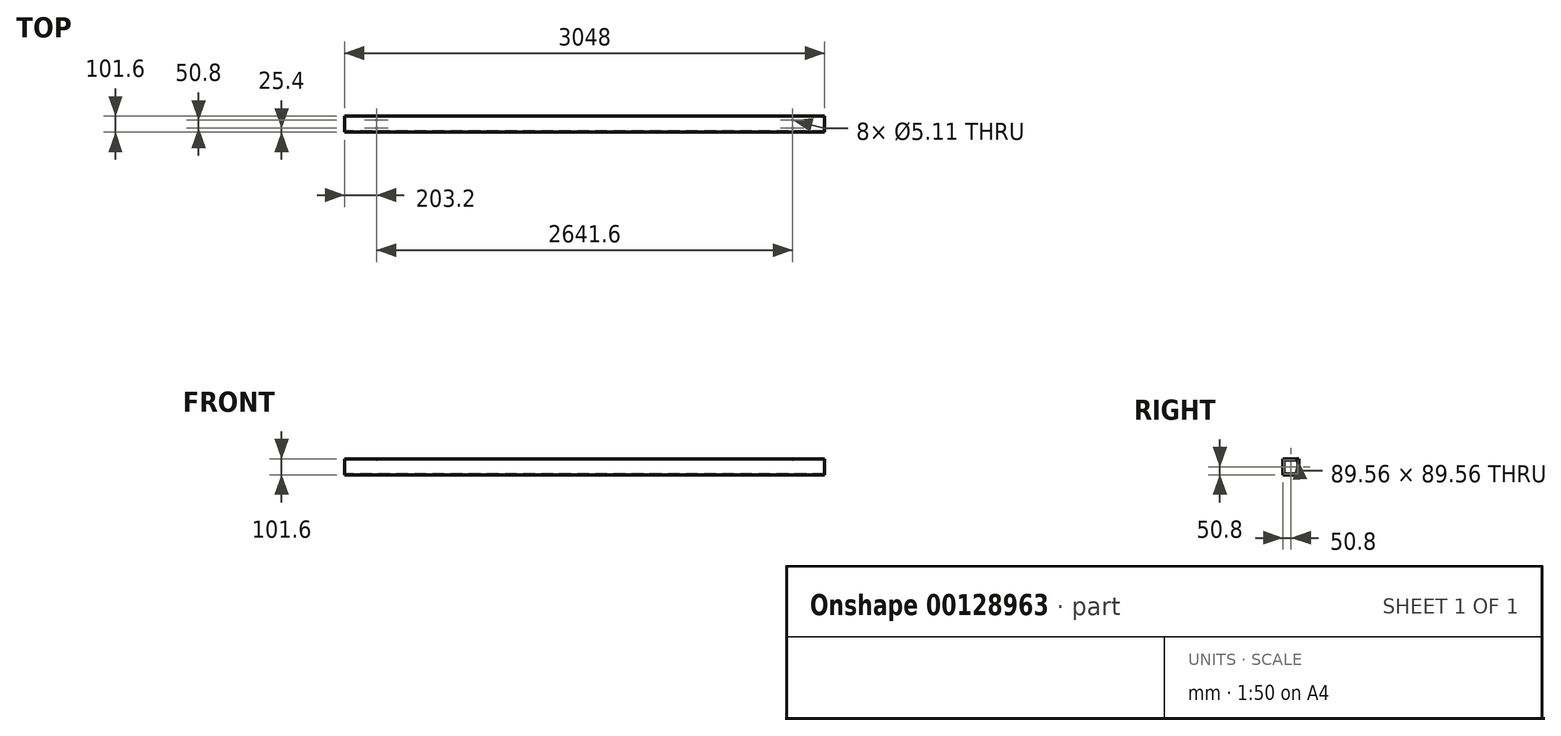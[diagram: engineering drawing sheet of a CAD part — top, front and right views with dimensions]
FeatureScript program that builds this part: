
annotation { "Feature Type Name" : "Feature", "Feature Type Description" : "" }
export const myFeature = defineFeature(function(context is Context, id is Id, definition is map)
    precondition{}
    {
        {
            var Q0;
            Q0=qCreatedBy(makeId("Right.planeOp"),FACE);
            var sketch = newSketch(context, id + "F0", { "sketchPlane" : qUnion([Q0])});
            skLineSegment(sketch, "E0.bottom", {"start": v(50.8, 50.8) * mm, "end": v(-50.8, 50.8) * mm});
            skLineSegment(sketch, "E0.top", {"start": v(50.8, -50.8) * mm, "end": v(-50.8, -50.8) * mm});
            skLineSegment(sketch, "E0.left", {"start": v(50.8, 50.8) * mm, "end": v(50.8, -50.8) * mm});
            skLineSegment(sketch, "E0.right", {"start": v(-50.8, 50.8) * mm, "end": v(-50.8, -50.8) * mm});
            skPoint(sketch, "E0.middle", {"position": v(0, 0) * mm});
            skLineSegment(sketch, "E1.bottom", {"start": v(44.78, 44.78) * mm, "end": v(-44.78, 44.78) * mm});
            skLineSegment(sketch, "E1.top", {"start": v(44.78, -44.78) * mm, "end": v(-44.78, -44.78) * mm});
            skLineSegment(sketch, "E1.left", {"start": v(44.78, 44.78) * mm, "end": v(44.78, -44.78) * mm});
            skLineSegment(sketch, "E1.right", {"start": v(-44.78, 44.78) * mm, "end": v(-44.78, -44.78) * mm});
            skSolve(sketch);
        }
        {
            var Q0;
            Q0=makeQuery(id+"F0.imprint","IMPRINT",FACE,{"disambiguationData":[TD([[makeQuery(id+"F0.imprint","IMPRINT",EDGE,{"derivedFrom":sQuery(id+"F0.wireOp",EDGE,"E0.bottom")}),1.0]])]});
            extrude(context, id + "F1", {"entities" : qUnion([Q0]), "endBound" : BoundingType.SYMMETRIC, "depth" : 3048 * mm});
        }
        {
            var Q0;
            Q0=makeQuery(id+"F1.opExtrude","SWEPT_FACE",FACE,{"disambiguationData":[OSD([sQuery(id+"F0.wireOp",EDGE,"E0.bottom")])]});
            var sketch = newSketch(context, id + "F2", { "sketchPlane" : qUnion([Q0])});
            skLineSegment(sketch, "E2", {"start": v(817.3, 0) * mm, "end": v(-691.9, 0) * mm});
            skLineSegment(sketch, "E3", {"start": v(0, -31.92) * mm, "end": v(0, 25.08) * mm});
            skPoint(sketch, "E3.endSnap0", {"position": v(0, 50.8) * mm});
            skPoint(sketch, "E4", {"position": v(1320.8, -25.4) * mm});
            skPoint(sketch, "E5", {"position": v(1320.8, 25.4) * mm});
            skPoint(sketch, "E6", {"position": v(-1320.8, -25.4) * mm});
            skPoint(sketch, "E7", {"position": v(-1320.8, 25.4) * mm});
            skLineSegment(sketch, "E8", {"start": v(-1320.8, -25.4) * mm, "end": v(-1320.8, 25.4) * mm});
            skLineSegment(sketch, "E9", {"start": v(-1320.8, -25.4) * mm, "end": v(1320.8, -25.4) * mm});
            skSolve(sketch);
        }
        {
            var Q0;
            Q0=sQuery(id+"F2.wireOp",VERTEX,"E7");
            var Q1;
            Q1=sQuery(id+"F2.wireOp",VERTEX,"E6");
            var Q2;
            Q2=sQuery(id+"F2.wireOp",VERTEX,"E5");
            var Q3;
            Q3=sQuery(id+"F2.wireOp",VERTEX,"E4");
            var Q4;
            Q4=makeQuery(id+"F1.opExtrude","SWEPT_BODY",BODY,{"disambiguationData":[OSD([sQuery(id+"F0.wireOp",EDGE,"E0.bottom"),sQuery(id+"F0.wireOp",EDGE,"E0.top"),sQuery(id+"F0.wireOp",EDGE,"E0.left"),sQuery(id+"F0.wireOp",EDGE,"E0.right"),sQuery(id+"F0.wireOp",EDGE,"E1.bottom"),sQuery(id+"F0.wireOp",EDGE,"E1.top"),sQuery(id+"F0.wireOp",EDGE,"E1.left"),sQuery(id+"F0.wireOp",EDGE,"E1.right")])]});
            hole(context, id + "F3", {"style" : HoleStyle.SIMPLE, "endStyle" : HoleEndStyle.THROUGH, "standardTappedOrClearance" : lookupTablePath({ "standard" : "ANSI", "engagement" : "75%", "pitch" : "20 tpi", "size" : "1/4", "type" : "Tapped" }), "standardBlindInLast" : lookupTablePath({ "standard" : "ANSI", "engagement" : "75%", "pitch" : "20 tpi", "size" : "1/4", "type" : "Tapped" }), "holeDiameter" : 5.1 * mm, "locations" : qUnion([Q0, Q1, Q2, Q3]), "scope" : qUnion([Q4]), "isTappedThrough" : true, "majorDiameter" : 6.35 * mm, "showTappedDepth" : true});
        }
    });
